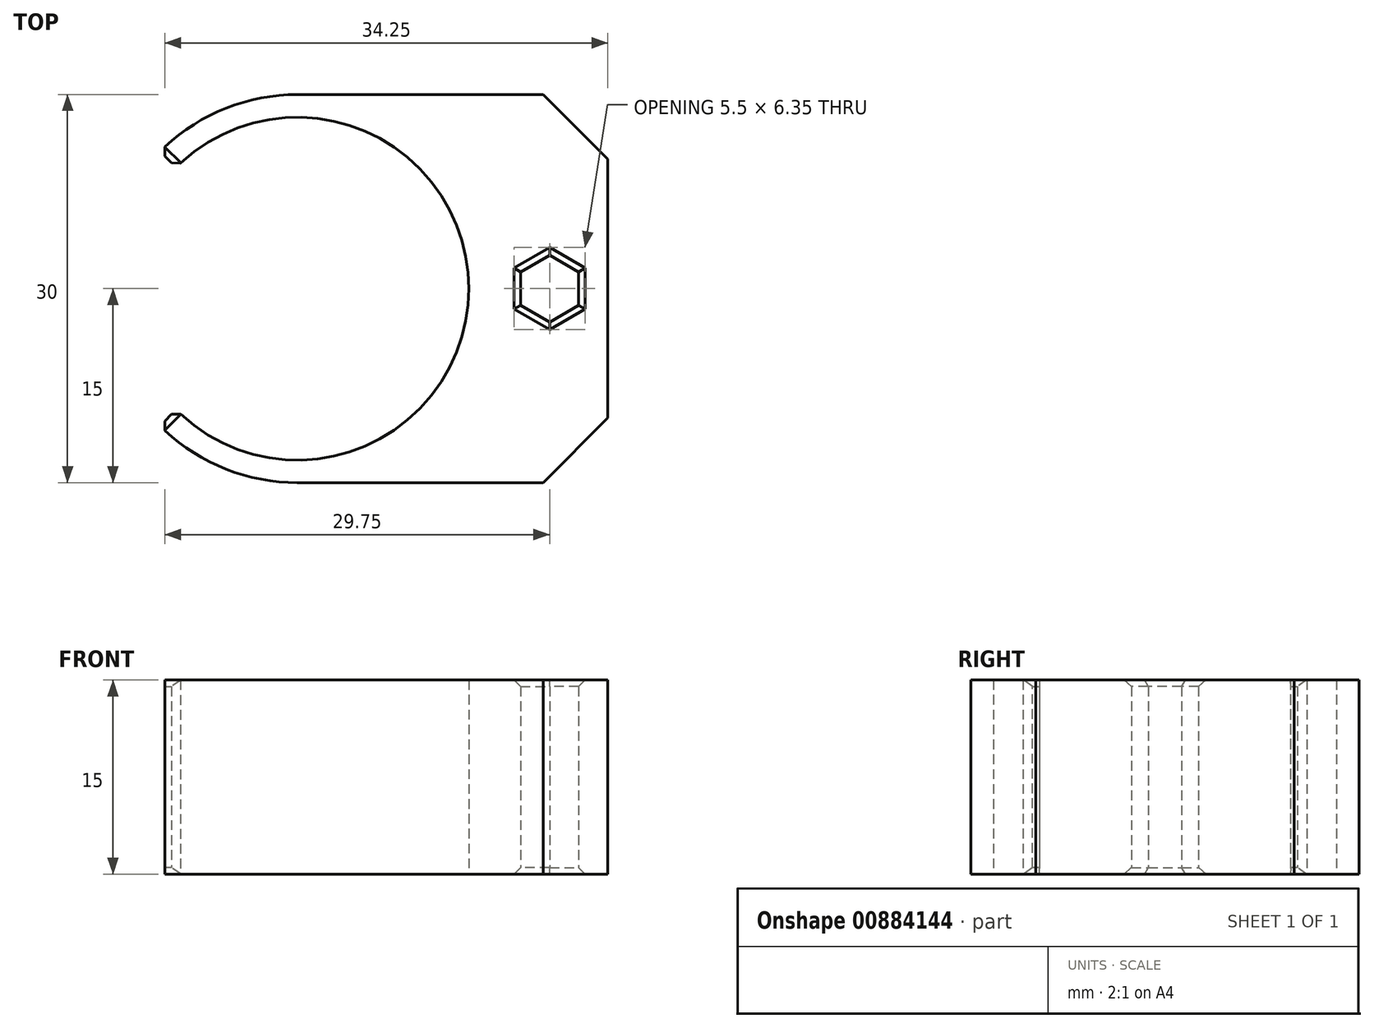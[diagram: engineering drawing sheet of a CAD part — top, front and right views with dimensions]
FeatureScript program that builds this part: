
annotation { "Feature Type Name" : "Feature", "Feature Type Description" : "" }
export const myFeature = defineFeature(function(context is Context, id is Id, definition is map)
    precondition{}
    {
        {
            var Q0;
            Q0=qCreatedBy(makeId("Top.planeOp"),FACE);
            var sketch = newSketch(context, id + "F0", { "sketchPlane" : qUnion([Q0])});
            skCircle(sketch, "E0", {"center": v(0, 0) * mm, "radius": 15 * mm});
            skCircle(sketch, "E1", {"center": v(0, 0) * mm, "radius": 13.25 * mm});
            skLineSegment(sketch, "E2", {"start": v(0, 15) * mm, "end": v(24, 15) * mm});
            skLineSegment(sketch, "E3", {"start": v(24, 15) * mm, "end": v(24, -15) * mm});
            skLineSegment(sketch, "E4", {"start": v(24, -15) * mm, "end": v(0, -15) * mm});
            skLineSegment(sketch, "E5", {"start": v(0, 0) * mm, "end": v(-17.5, 17.5) * mm});
            skLineSegment(sketch, "E6", {"start": v(-17.5, 17.5) * mm, "end": v(-17.5, -17.5) * mm});
            skLineSegment(sketch, "E7", {"start": v(-17.5, -17.5) * mm, "end": v(0, 0) * mm});
            skCircle(sketch, "E8.cCircle", {"center": v(19.5, 0) * mm, "radius": 2.25 * mm, "construction": true});
            skLineSegment(sketch, "E8.0", {"start": v(17.25, -1.3) * mm, "end": v(17.25, 1.3) * mm});
            skLineSegment(sketch, "E8.1", {"start": v(17.25, 1.3) * mm, "end": v(19.5, 2.6) * mm});
            skLineSegment(sketch, "E8.2", {"start": v(19.5, 2.6) * mm, "end": v(21.75, 1.3) * mm});
            skLineSegment(sketch, "E8.3", {"start": v(21.75, 1.3) * mm, "end": v(21.75, -1.3) * mm});
            skLineSegment(sketch, "E8.4", {"start": v(21.75, -1.3) * mm, "end": v(19.5, -2.6) * mm});
            skLineSegment(sketch, "E8.5", {"start": v(19.5, -2.6) * mm, "end": v(17.25, -1.3) * mm});
            skPoint(sketch, "E8.0.midPoint", {"position": v(17.25, 0) * mm});
            skSolve(sketch);
        }
        {
            var Q0;
            {var subQ0=sQuery(id+"F0.wireOp",EDGE,"E0");var subQ1=makeQuery(id+"F0.imprint","INTERSECT",VERTEX,{"derivedFrom":[subQ0,sQuery(id+"F0.wireOp",EDGE,"E2")]});Q0=makeQuery(id+"F0.imprint","IMPRINT",FACE,{"disambiguationData":[TD([[makeQuery(id+"F0.imprint","IMPRINT",EDGE,{"disambiguationData":[TD([[subQ1,-1.0]])],"derivedFrom":subQ0}),1.0]])]});}
            var Q1;
            {var subQ0=sQuery(id+"F0.wireOp",EDGE,"E2");Q1=makeQuery(id+"F0.imprint","IMPRINT",FACE,{"disambiguationData":[TD([[makeQuery(id+"F0.imprint","IMPRINT",EDGE,{"derivedFrom":subQ0}),-1.0]])]});}
            extrude(context, id + "F1", {"entities" : qUnion([Q0, Q1]), "depth" : 15 * mm, "offsetDistance" : 25 * mm});
        }
        {
            var Q0;
            Q0=makeQuery(id+"F1.opExtrude","SWEPT_FACE",FACE,{"disambiguationData":[OSD([sQuery(id+"F0.wireOp",EDGE,"E5")])]});
            var Q1;
            Q1=makeQuery(id+"F1.opExtrude","SWEPT_FACE",FACE,{"disambiguationData":[OSD([sQuery(id+"F0.wireOp",EDGE,"E7")])]});
            chamfer(context, id + "F2", {"entities" : qUnion([Q0, Q1]), "width" : 0.5 * mm, "tangentPropagation" : true});
        }
        {
            var Q0;
            Q0=makeQuery(id+"F1.opExtrude","SWEPT_EDGE",EDGE,{"disambiguationData":[OSD([sQuery(id+"F0.wireOp",EDGE,"E3"),sQuery(id+"F0.wireOp",EDGE,"E4")])]});
            var Q1;
            Q1=makeQuery(id+"F1.opExtrude","SWEPT_EDGE",EDGE,{"disambiguationData":[OSD([sQuery(id+"F0.wireOp",EDGE,"E2"),sQuery(id+"F0.wireOp",EDGE,"E3")])]});
            chamfer(context, id + "F3", {"entities" : qUnion([Q0, Q1]), "width" : 5 * mm, "tangentPropagation" : true});
        }
        {
            var Q0;
            Q0=makeQuery(id+"F1.opExtrude","CAP_EDGE",EDGE,{"disambiguationData":[OSD([sQuery(id+"F0.wireOp",EDGE,"E8.1")])],"isStart":false});
            var Q1;
            Q1=makeQuery(id+"F1.opExtrude","CAP_EDGE",EDGE,{"disambiguationData":[OSD([sQuery(id+"F0.wireOp",EDGE,"E8.2")])],"isStart":false});
            var Q2;
            Q2=makeQuery(id+"F1.opExtrude","CAP_EDGE",EDGE,{"disambiguationData":[OSD([sQuery(id+"F0.wireOp",EDGE,"E8.3")])],"isStart":false});
            var Q3;
            Q3=makeQuery(id+"F1.opExtrude","CAP_EDGE",EDGE,{"disambiguationData":[OSD([sQuery(id+"F0.wireOp",EDGE,"E8.4")])],"isStart":false});
            var Q4;
            Q4=makeQuery(id+"F1.opExtrude","CAP_EDGE",EDGE,{"disambiguationData":[OSD([sQuery(id+"F0.wireOp",EDGE,"E8.5")])],"isStart":false});
            var Q5;
            Q5=makeQuery(id+"F1.opExtrude","CAP_EDGE",EDGE,{"disambiguationData":[OSD([sQuery(id+"F0.wireOp",EDGE,"E8.0")])],"isStart":false});
            var Q6;
            Q6=makeQuery(id+"F1.opExtrude","CAP_EDGE",EDGE,{"disambiguationData":[OSD([sQuery(id+"F0.wireOp",EDGE,"E8.2")])],"isStart":true});
            var Q7;
            Q7=makeQuery(id+"F1.opExtrude","CAP_EDGE",EDGE,{"disambiguationData":[OSD([sQuery(id+"F0.wireOp",EDGE,"E8.3")])],"isStart":true});
            var Q8;
            Q8=makeQuery(id+"F1.opExtrude","CAP_EDGE",EDGE,{"disambiguationData":[OSD([sQuery(id+"F0.wireOp",EDGE,"E8.4")])],"isStart":true});
            var Q9;
            Q9=makeQuery(id+"F1.opExtrude","CAP_EDGE",EDGE,{"disambiguationData":[OSD([sQuery(id+"F0.wireOp",EDGE,"E8.5")])],"isStart":true});
            var Q10;
            Q10=makeQuery(id+"F1.opExtrude","CAP_EDGE",EDGE,{"disambiguationData":[OSD([sQuery(id+"F0.wireOp",EDGE,"E8.0")])],"isStart":true});
            var Q11;
            Q11=makeQuery(id+"F1.opExtrude","CAP_EDGE",EDGE,{"disambiguationData":[OSD([sQuery(id+"F0.wireOp",EDGE,"E8.1")])],"isStart":true});
            chamfer(context, id + "F4", {"entities" : qUnion([Q0, Q1, Q2, Q3, Q4, Q5, Q6, Q7, Q8, Q9, Q10, Q11]), "width" : 0.5 * mm, "tangentPropagation" : true});
        }
    });
